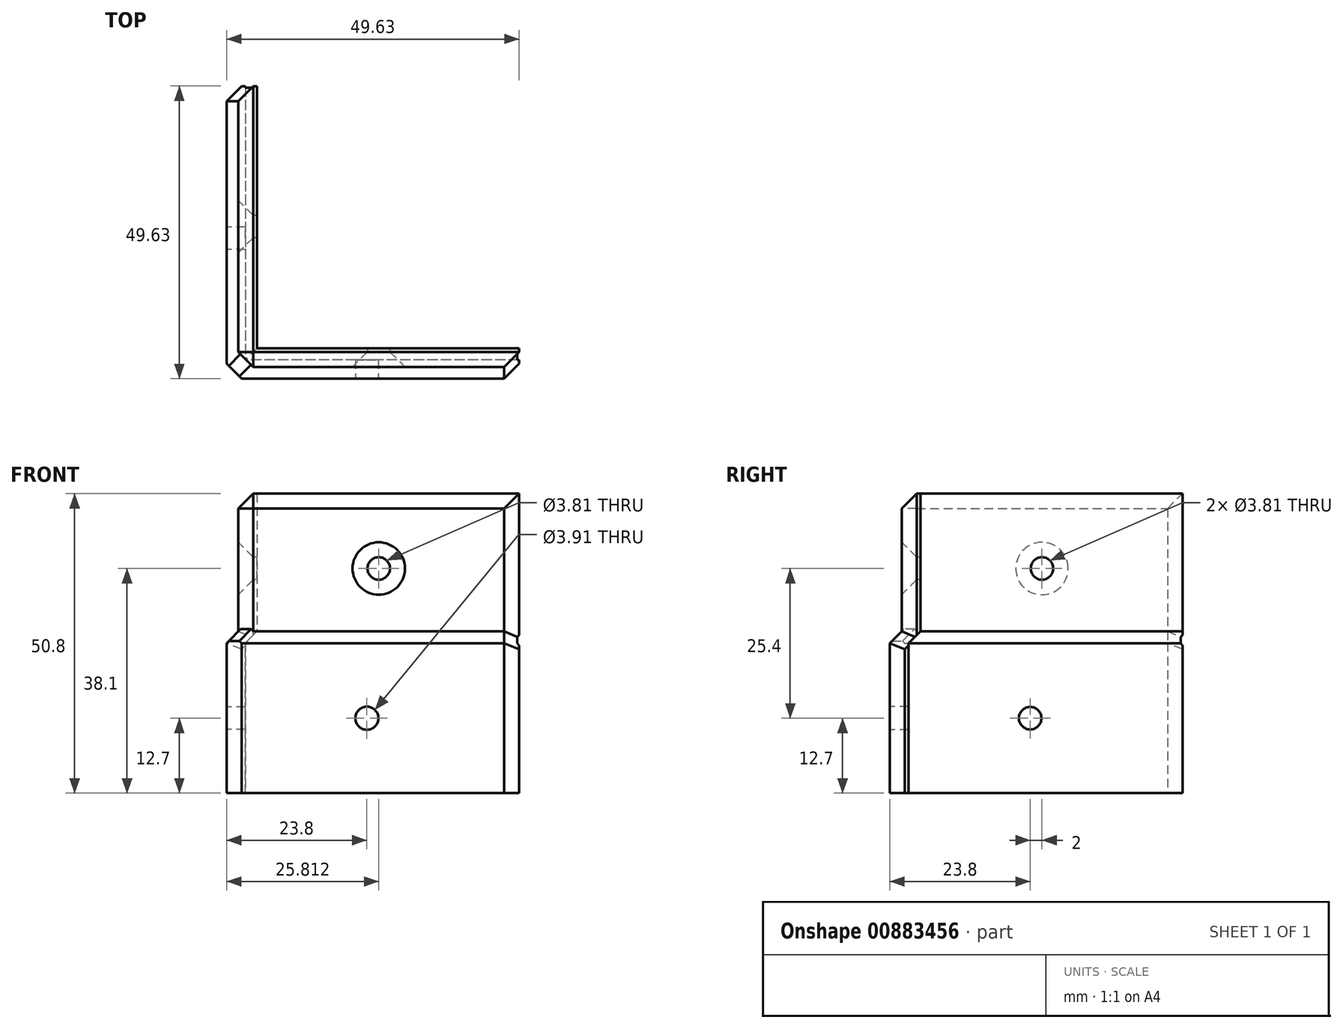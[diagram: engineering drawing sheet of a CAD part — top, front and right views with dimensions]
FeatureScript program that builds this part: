
annotation { "Feature Type Name" : "Feature", "Feature Type Description" : "" }
export const myFeature = defineFeature(function(context is Context, id is Id, definition is map)
    precondition{}
    {
        {
            var Q0;
            Q0=qCreatedBy(makeId("Top.planeOp"),FACE);
            var sketch = newSketch(context, id + "F0", { "sketchPlane" : qUnion([Q0])});
            skLineSegment(sketch, "E0.bottom", {"start": v(0, 0) * mm, "end": v(47.62, 0) * mm});
            skLineSegment(sketch, "E0.top", {"start": v(0, 47.63) * mm, "end": v(3.17, 47.63) * mm});
            skLineSegment(sketch, "E0.left", {"start": v(0, 0) * mm, "end": v(0, 47.63) * mm});
            skLineSegment(sketch, "E0.right", {"start": v(47.63, 0) * mm, "end": v(47.63, 3.18) * mm});
            skLineSegment(sketch, "E1.top", {"start": v(47.63, 3.18) * mm, "end": v(3.17, 3.17) * mm});
            skLineSegment(sketch, "E1.right", {"start": v(3.17, 47.63) * mm, "end": v(3.17, 3.18) * mm});
            skSolve(sketch);
        }
        {
            var Q0;
            Q0=qSketchRegion(id+"F0",true);
            extrude(context, id + "F1", {"entities" : qUnion([Q0]), "depth" : 25.4 * mm, "offsetDistance" : 25.4 * mm});
        }
        {
            var Q0;
            Q0=makeQuery(id+"F1.opExtrude","CAP_FACE",FACE,{"disambiguationData":[OSD([sQuery(id+"F0.wireOp",EDGE,"E0.bottom"),sQuery(id+"F0.wireOp",EDGE,"E0.top"),sQuery(id+"F0.wireOp",EDGE,"E0.left"),sQuery(id+"F0.wireOp",EDGE,"E0.right"),sQuery(id+"F0.wireOp",EDGE,"E1.top"),sQuery(id+"F0.wireOp",EDGE,"E1.right")])],"isStart":false});
            var sketch = newSketch(context, id + "F2", { "sketchPlane" : qUnion([Q0])});
            skLineSegment(sketch, "E2.bottom", {"start": v(5.17, 49.62) * mm, "end": v(2, 49.62) * mm});
            skLineSegment(sketch, "E2.top", {"start": v(49.63, 2) * mm, "end": v(2, 2) * mm});
            skLineSegment(sketch, "E2.left", {"start": v(49.63, 5.17) * mm, "end": v(49.63, 2) * mm});
            skLineSegment(sketch, "E2.right", {"start": v(2, 49.63) * mm, "end": v(2, 2) * mm});
            skLineSegment(sketch, "E3.top", {"start": v(49.63, 5.17) * mm, "end": v(5.17, 5.17) * mm});
            skLineSegment(sketch, "E3.right", {"start": v(5.17, 49.63) * mm, "end": v(5.17, 5.17) * mm});
            skSolve(sketch);
        }
        {
            var Q0;
            Q0=qSketchRegion(id+"F2",true);
            extrude(context, id + "F3", {"entities" : qUnion([Q0]), "operationType" : NewBodyOperationType.ADD, "depth" : 25.4 * mm, "offsetDistance" : 25.4 * mm});
        }
        {
            var Q0;
            Q0=makeQuery(id+"F1.opExtrude","SWEPT_FACE",FACE,{"disambiguationData":[OSD([sQuery(id+"F0.wireOp",EDGE,"E0.bottom")])]});
            var sketch = newSketch(context, id + "F4", { "sketchPlane" : qUnion([Q0])});
            skCircle(sketch, "E4", {"center": v(23.8, 12.7) * mm, "radius": 1.96 * mm});
            skCircle(sketch, "E5", {"center": v(25.81, 38.1) * mm, "radius": 1.9 * mm});
            skSolve(sketch);
        }
        {
            var Q0;
            Q0=qSketchRegion(id+"F4",true);
            extrude(context, id + "F5", {"entities" : qUnion([Q0]), "operationType" : NewBodyOperationType.REMOVE, "oppositeDirection" : true, "depth" : 25.4 * mm, "offsetDistance" : 25.4 * mm});
        }
        {
            var Q0;
            Q0=makeQuery(id+"F1.opExtrude","SWEPT_FACE",FACE,{"disambiguationData":[OSD([sQuery(id+"F0.wireOp",EDGE,"E0.left")])]});
            var sketch = newSketch(context, id + "F6", { "sketchPlane" : qUnion([Q0])});
            skCircle(sketch, "E6", {"center": v(-23.8, 12.7) * mm, "radius": 1.9 * mm});
            skCircle(sketch, "E7", {"center": v(-25.8, 38.1) * mm, "radius": 1.9 * mm});
            skSolve(sketch);
        }
        {
            var Q0;
            Q0=qSketchRegion(id+"F6",true);
            extrude(context, id + "F7", {"entities" : qUnion([Q0]), "operationType" : NewBodyOperationType.REMOVE, "oppositeDirection" : true, "depth" : 25.4 * mm, "offsetDistance" : 25.4 * mm});
        }
        {
            var Q0;
            Q0=makeQuery(id+"F7.boolean.opBoolean","COPY",EDGE,{"derivedFrom":makeQuery(id+"F7.opExtrude","CAP_EDGE",EDGE,{"disambiguationData":[OSD([sQuery(id+"F6.wireOp",EDGE,"E6")])],"isStart":true})});
            var Q1;
            Q1=makeQuery(id+"F7.boolean.opBoolean","INTERSECT",EDGE,{"derivedFrom":[makeQuery(id+"F3.opExtrude","SWEPT_FACE",FACE,{"disambiguationData":[OSD([sQuery(id+"F2.wireOp",EDGE,"E2.right")])]}),makeQuery(id+"F7.opExtrude","SWEPT_FACE",FACE,{"disambiguationData":[OSD([sQuery(id+"F6.wireOp",EDGE,"E7")])]})]});
            var Q2;
            Q2=makeQuery(id+"F5.boolean.opBoolean","INTERSECT",EDGE,{"derivedFrom":[makeQuery(id+"F3.opExtrude","SWEPT_FACE",FACE,{"disambiguationData":[OSD([sQuery(id+"F2.wireOp",EDGE,"E2.top")])]}),makeQuery(id+"F5.opExtrude","SWEPT_FACE",FACE,{"disambiguationData":[OSD([sQuery(id+"F4.wireOp",EDGE,"E5")])]})]});
            var Q3;
            Q3=makeQuery(id+"F5.boolean.opBoolean","COPY",EDGE,{"derivedFrom":makeQuery(id+"F5.opExtrude","CAP_EDGE",EDGE,{"disambiguationData":[OSD([sQuery(id+"F4.wireOp",EDGE,"E4")])],"isStart":true})});
            chamfer(context, id + "F8", {"entities" : qUnion([Q0, Q1, Q2, Q3]), "width" : 2.54 * mm, "tangentPropagation" : true});
        }
        {
            var Q0;
            Q0=makeQuery(id+"F1.opExtrude","SWEPT_FACE",FACE,{"disambiguationData":[OSD([sQuery(id+"F0.wireOp",EDGE,"E0.top")])]});
            var Q1;
            Q1=makeQuery(id+"F3.opExtrude","SWEPT_FACE",FACE,{"disambiguationData":[OSD([sQuery(id+"F2.wireOp",EDGE,"E2.bottom")])]});
            extrude(context, id + "F9", {"entities" : qUnion([Q0]), "operationType" : NewBodyOperationType.ADD, "endBound" : BoundingType.UP_TO_SURFACE, "depth" : 25.4 * mm, "endBoundEntityFace" : qUnion([Q1]), "offsetDistance" : 25.4 * mm});
        }
        {
            var Q0;
            Q0=makeQuery(id+"F1.opExtrude","SWEPT_FACE",FACE,{"disambiguationData":[OSD([sQuery(id+"F0.wireOp",EDGE,"E0.right")])]});
            var Q1;
            Q1=makeQuery(id+"F3.opExtrude","SWEPT_FACE",FACE,{"disambiguationData":[OSD([sQuery(id+"F2.wireOp",EDGE,"E2.left")])]});
            extrude(context, id + "F10", {"entities" : qUnion([Q0]), "operationType" : NewBodyOperationType.ADD, "endBound" : BoundingType.UP_TO_SURFACE, "depth" : 25.4 * mm, "endBoundEntityFace" : qUnion([Q1]), "offsetDistance" : 25.4 * mm});
        }
        {
            var Q0;
            {var subQ0=sQuery(id+"F2.wireOp",EDGE,"E2.top");var subQ2=makeQuery(id+"F3.opExtrude","CAP_EDGE",EDGE,{"disambiguationData":[OSD([subQ0])],"isStart":true});Q0=makeQuery(id+"F10.boolean.opBoolean","MERGE",EDGE,{"derivedFrom":[makeQuery(id+"F3.boolean.opBoolean","SPLIT",EDGE,{"disambiguationData":[topologyDisambiguationEdgeConnected([makeQuery(id+"F3.opExtrude","CAP_FACE",FACE,{"disambiguationData":[OSD([sQuery(id+"F2.wireOp",EDGE,"E2.bottom"),subQ0,sQuery(id+"F2.wireOp",EDGE,"E2.left"),sQuery(id+"F2.wireOp",EDGE,"E2.right"),sQuery(id+"F2.wireOp",EDGE,"E3.top"),sQuery(id+"F2.wireOp",EDGE,"E3.right")])],"isStart":true})])],"derivedFrom":subQ2}),makeQuery(id+"F3.boolean.opBoolean","SPLIT",EDGE,{"disambiguationData":[topologyDisambiguationEdgeConnected([makeQuery(id+"F1.opExtrude","CAP_FACE",FACE,{"disambiguationData":[OSD([sQuery(id+"F0.wireOp",EDGE,"E0.bottom"),sQuery(id+"F0.wireOp",EDGE,"E0.top"),sQuery(id+"F0.wireOp",EDGE,"E0.left"),sQuery(id+"F0.wireOp",EDGE,"E0.right"),sQuery(id+"F0.wireOp",EDGE,"E1.top"),sQuery(id+"F0.wireOp",EDGE,"E1.right")])],"isStart":false})])],"derivedFrom":subQ2})]});}
            var Q1;
            {var subQ0=sQuery(id+"F2.wireOp",EDGE,"E2.right");var subQ2=makeQuery(id+"F3.opExtrude","CAP_EDGE",EDGE,{"disambiguationData":[OSD([subQ0])],"isStart":true});Q1=makeQuery(id+"F9.boolean.opBoolean","MERGE",EDGE,{"derivedFrom":[makeQuery(id+"F3.boolean.opBoolean","SPLIT",EDGE,{"disambiguationData":[topologyDisambiguationEdgeConnected([makeQuery(id+"F3.opExtrude","CAP_FACE",FACE,{"disambiguationData":[OSD([sQuery(id+"F2.wireOp",EDGE,"E2.bottom"),sQuery(id+"F2.wireOp",EDGE,"E2.top"),sQuery(id+"F2.wireOp",EDGE,"E2.left"),subQ0,sQuery(id+"F2.wireOp",EDGE,"E3.top"),sQuery(id+"F2.wireOp",EDGE,"E3.right")])],"isStart":true})])],"derivedFrom":subQ2}),makeQuery(id+"F3.boolean.opBoolean","SPLIT",EDGE,{"disambiguationData":[topologyDisambiguationEdgeConnected([makeQuery(id+"F1.opExtrude","CAP_FACE",FACE,{"disambiguationData":[OSD([sQuery(id+"F0.wireOp",EDGE,"E0.bottom"),sQuery(id+"F0.wireOp",EDGE,"E0.top"),sQuery(id+"F0.wireOp",EDGE,"E0.left"),sQuery(id+"F0.wireOp",EDGE,"E0.right"),sQuery(id+"F0.wireOp",EDGE,"E1.top"),sQuery(id+"F0.wireOp",EDGE,"E1.right")])],"isStart":false})])],"derivedFrom":subQ2})]});}
            var Q2;
            Q2=makeQuery(id+"F3.opExtrude","CAP_EDGE",EDGE,{"disambiguationData":[OSD([sQuery(id+"F2.wireOp",EDGE,"E3.top")])],"isStart":true});
            var Q3;
            Q3=makeQuery(id+"F3.opExtrude","CAP_EDGE",EDGE,{"disambiguationData":[OSD([sQuery(id+"F2.wireOp",EDGE,"E3.right")])],"isStart":true});
            chamfer(context, id + "F11", {"entities" : qUnion([Q0, Q1, Q2, Q3]), "width" : 2.03 * mm, "tangentPropagation" : true});
        }
        {
            var Q0;
            Q0=makeQuery(id+"F3.opExtrude","SWEPT_EDGE",EDGE,{"disambiguationData":[OSD([sQuery(id+"F2.wireOp",EDGE,"E2.top"),sQuery(id+"F2.wireOp",EDGE,"E2.left")])]});
            var Q1;
            {var subQ0=sQuery(id+"F0.wireOp",EDGE,"E0.right");var subQ1=sQuery(id+"F2.wireOp",EDGE,"E2.left");var subQ2=sQuery(id+"F2.wireOp",EDGE,"E2.top");var subQ4=makeQuery(id+"F3.opExtrude","CAP_EDGE",EDGE,{"disambiguationData":[OSD([subQ2])],"isStart":true});Q1=makeQuery(id+"F11.opChamfer","BLEND_EDGE",EDGE,{"blendedFrom":[makeQuery(id+"F10.boolean.opBoolean","MERGE",EDGE,{"derivedFrom":[makeQuery(id+"F3.boolean.opBoolean","SPLIT",EDGE,{"disambiguationData":[topologyDisambiguationEdgeConnected([makeQuery(id+"F3.opExtrude","CAP_FACE",FACE,{"disambiguationData":[OSD([sQuery(id+"F2.wireOp",EDGE,"E2.bottom"),subQ2,subQ1,sQuery(id+"F2.wireOp",EDGE,"E2.right"),sQuery(id+"F2.wireOp",EDGE,"E3.top"),sQuery(id+"F2.wireOp",EDGE,"E3.right")])],"isStart":true})])],"derivedFrom":subQ4}),makeQuery(id+"F3.boolean.opBoolean","SPLIT",EDGE,{"disambiguationData":[topologyDisambiguationEdgeConnected([makeQuery(id+"F1.opExtrude","CAP_FACE",FACE,{"disambiguationData":[OSD([sQuery(id+"F0.wireOp",EDGE,"E0.bottom"),sQuery(id+"F0.wireOp",EDGE,"E0.top"),sQuery(id+"F0.wireOp",EDGE,"E0.left"),subQ0,sQuery(id+"F0.wireOp",EDGE,"E1.top"),sQuery(id+"F0.wireOp",EDGE,"E1.right")])],"isStart":false})])],"derivedFrom":subQ4})]}),makeQuery(id+"F10.boolean.opBoolean","MERGE",FACE,{"derivedFrom":[makeQuery(id+"F3.opExtrude","SWEPT_FACE",FACE,{"disambiguationData":[OSD([subQ1])]}),makeQuery(id+"F10.opExtrude","CAP_FACE",FACE,{"disambiguationData":[OSD([subQ0])],"isStart":false})]})],"blendedInto":[makeQuery(id+"F10.boolean.opBoolean","MERGE",FACE,{"derivedFrom":[makeQuery(id+"F3.opExtrude","SWEPT_FACE",FACE,{"disambiguationData":[OSD([subQ1])]}),makeQuery(id+"F10.opExtrude","CAP_FACE",FACE,{"disambiguationData":[OSD([subQ0])],"isStart":false})]})]});}
            var Q2;
            Q2=makeQuery(id+"F10.opExtrude","CAP_EDGE",EDGE,{"disambiguationData":[OSD([sQuery(id+"F0.wireOp",EDGE,"E0.bottom"),sQuery(id+"F0.wireOp",EDGE,"E0.right")])],"isStart":false});
            var Q3;
            Q3=makeQuery(id+"F3.opExtrude","SWEPT_EDGE",EDGE,{"disambiguationData":[OSD([sQuery(id+"F2.wireOp",EDGE,"E2.bottom"),sQuery(id+"F2.wireOp",EDGE,"E2.right")])]});
            var Q4;
            {var subQ0=sQuery(id+"F0.wireOp",EDGE,"E0.top");var subQ1=sQuery(id+"F2.wireOp",EDGE,"E2.bottom");var subQ2=sQuery(id+"F2.wireOp",EDGE,"E2.right");var subQ4=makeQuery(id+"F3.opExtrude","CAP_EDGE",EDGE,{"disambiguationData":[OSD([subQ2])],"isStart":true});Q4=makeQuery(id+"F11.opChamfer","BLEND_EDGE",EDGE,{"blendedFrom":[makeQuery(id+"F9.boolean.opBoolean","MERGE",EDGE,{"derivedFrom":[makeQuery(id+"F3.boolean.opBoolean","SPLIT",EDGE,{"disambiguationData":[topologyDisambiguationEdgeConnected([makeQuery(id+"F3.opExtrude","CAP_FACE",FACE,{"disambiguationData":[OSD([subQ1,sQuery(id+"F2.wireOp",EDGE,"E2.top"),sQuery(id+"F2.wireOp",EDGE,"E2.left"),subQ2,sQuery(id+"F2.wireOp",EDGE,"E3.top"),sQuery(id+"F2.wireOp",EDGE,"E3.right")])],"isStart":true})])],"derivedFrom":subQ4}),makeQuery(id+"F3.boolean.opBoolean","SPLIT",EDGE,{"disambiguationData":[topologyDisambiguationEdgeConnected([makeQuery(id+"F1.opExtrude","CAP_FACE",FACE,{"disambiguationData":[OSD([sQuery(id+"F0.wireOp",EDGE,"E0.bottom"),subQ0,sQuery(id+"F0.wireOp",EDGE,"E0.left"),sQuery(id+"F0.wireOp",EDGE,"E0.right"),sQuery(id+"F0.wireOp",EDGE,"E1.top"),sQuery(id+"F0.wireOp",EDGE,"E1.right")])],"isStart":false})])],"derivedFrom":subQ4})]}),makeQuery(id+"F9.boolean.opBoolean","MERGE",FACE,{"derivedFrom":[makeQuery(id+"F3.opExtrude","SWEPT_FACE",FACE,{"disambiguationData":[OSD([subQ1])]}),makeQuery(id+"F9.opExtrude","CAP_FACE",FACE,{"disambiguationData":[OSD([subQ0])],"isStart":false})]})],"blendedInto":[makeQuery(id+"F9.boolean.opBoolean","MERGE",FACE,{"derivedFrom":[makeQuery(id+"F3.opExtrude","SWEPT_FACE",FACE,{"disambiguationData":[OSD([subQ1])]}),makeQuery(id+"F9.opExtrude","CAP_FACE",FACE,{"disambiguationData":[OSD([subQ0])],"isStart":false})]})]});}
            var Q5;
            Q5=makeQuery(id+"F9.opExtrude","CAP_EDGE",EDGE,{"disambiguationData":[OSD([sQuery(id+"F0.wireOp",EDGE,"E0.top"),sQuery(id+"F0.wireOp",EDGE,"E0.left")])],"isStart":false});
            var Q6;
            Q6=makeQuery(id+"F3.opExtrude","CAP_EDGE",EDGE,{"disambiguationData":[OSD([sQuery(id+"F2.wireOp",EDGE,"E2.right")])],"isStart":false});
            var Q7;
            Q7=makeQuery(id+"F3.opExtrude","CAP_EDGE",EDGE,{"disambiguationData":[OSD([sQuery(id+"F2.wireOp",EDGE,"E2.top")])],"isStart":false});
            var Q8;
            Q8=makeQuery(id+"F3.opExtrude","SWEPT_EDGE",EDGE,{"disambiguationData":[OSD([sQuery(id+"F2.wireOp",EDGE,"E2.top"),sQuery(id+"F2.wireOp",EDGE,"E2.right")])]});
            var Q9;
            Q9=makeQuery(id+"F1.opExtrude","SWEPT_EDGE",EDGE,{"disambiguationData":[OSD([sQuery(id+"F0.wireOp",EDGE,"E0.bottom"),sQuery(id+"F0.wireOp",EDGE,"E0.left")])]});
            var Q10;
            {var subQ0=makeQuery(id+"F1.opExtrude","CAP_FACE",FACE,{"disambiguationData":[OSD([sQuery(id+"F0.wireOp",EDGE,"E0.bottom"),sQuery(id+"F0.wireOp",EDGE,"E0.top"),sQuery(id+"F0.wireOp",EDGE,"E0.left"),sQuery(id+"F0.wireOp",EDGE,"E0.right"),sQuery(id+"F0.wireOp",EDGE,"E1.top"),sQuery(id+"F0.wireOp",EDGE,"E1.right")])],"isStart":false});var subQ1=sQuery(id+"F2.wireOp",EDGE,"E2.top");var subQ3=makeQuery(id+"F3.opExtrude","CAP_EDGE",EDGE,{"disambiguationData":[OSD([subQ1])],"isStart":true});var subQ4=sQuery(id+"F2.wireOp",EDGE,"E2.right");var subQ5=makeQuery(id+"F3.opExtrude","CAP_FACE",FACE,{"disambiguationData":[OSD([sQuery(id+"F2.wireOp",EDGE,"E2.bottom"),subQ1,sQuery(id+"F2.wireOp",EDGE,"E2.left"),subQ4,sQuery(id+"F2.wireOp",EDGE,"E3.top"),sQuery(id+"F2.wireOp",EDGE,"E3.right")])],"isStart":true});var subQ7=makeQuery(id+"F3.opExtrude","CAP_EDGE",EDGE,{"disambiguationData":[OSD([subQ4])],"isStart":true});Q10=makeQuery(id+"F11.opChamfer","BLEND_EDGE",EDGE,{"blendedFrom":[makeQuery(id+"F9.boolean.opBoolean","MERGE",EDGE,{"derivedFrom":[makeQuery(id+"F3.boolean.opBoolean","SPLIT",EDGE,{"disambiguationData":[topologyDisambiguationEdgeConnected([subQ5])],"derivedFrom":subQ7}),makeQuery(id+"F3.boolean.opBoolean","SPLIT",EDGE,{"disambiguationData":[topologyDisambiguationEdgeConnected([subQ0])],"derivedFrom":subQ7})]}),makeQuery(id+"F10.boolean.opBoolean","MERGE",EDGE,{"derivedFrom":[makeQuery(id+"F3.boolean.opBoolean","SPLIT",EDGE,{"disambiguationData":[topologyDisambiguationEdgeConnected([subQ5])],"derivedFrom":subQ3}),makeQuery(id+"F3.boolean.opBoolean","SPLIT",EDGE,{"disambiguationData":[topologyDisambiguationEdgeConnected([subQ0])],"derivedFrom":subQ3})]})],"blendedInto":[]});}
            chamfer(context, id + "F12", {"entities" : qUnion([Q0, Q1, Q2, Q3, Q4, Q5, Q6, Q7, Q8, Q9, Q10]), "width" : 2.54 * mm, "tangentPropagation" : true});
        }
    });
